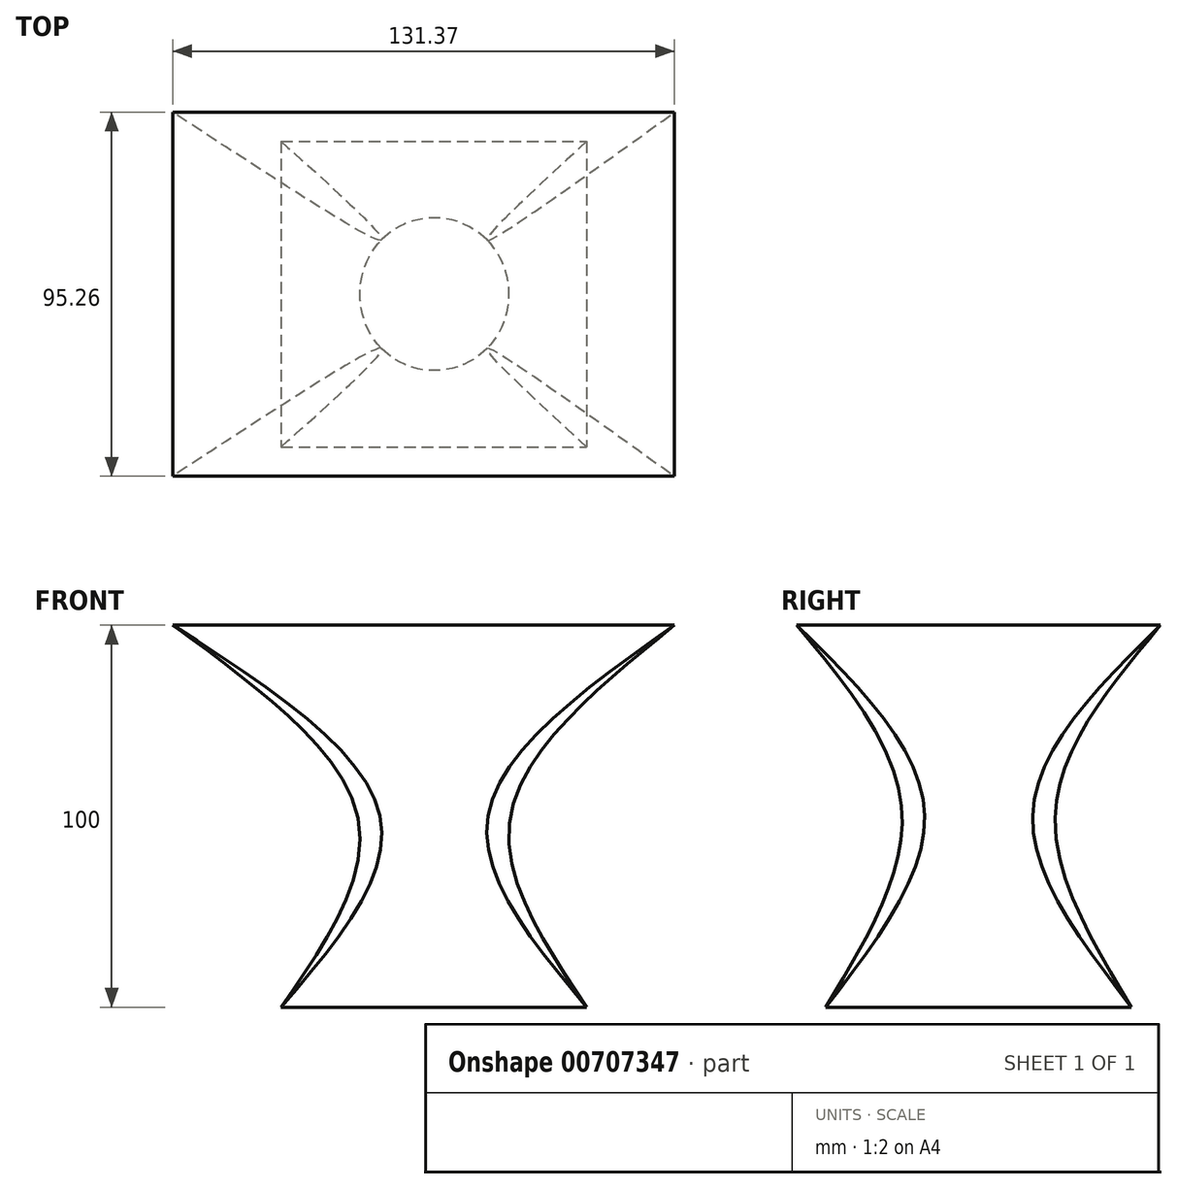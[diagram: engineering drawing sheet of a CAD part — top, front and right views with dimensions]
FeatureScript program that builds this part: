
annotation { "Feature Type Name" : "Feature", "Feature Type Description" : "" }
export const myFeature = defineFeature(function(context is Context, id is Id, definition is map)
    precondition{}
    {
        {
            var Q0;
            Q0=qCreatedBy(makeId("Top.planeOp"),FACE);
            var sketch = newSketch(context, id + "F0", { "sketchPlane" : qUnion([Q0])});
            skLineSegment(sketch, "E0.bottom", {"start": v(-40, 40) * mm, "end": v(40, 40) * mm});
            skLineSegment(sketch, "E0.top", {"start": v(-40, -40) * mm, "end": v(40, -40) * mm});
            skLineSegment(sketch, "E0.left", {"start": v(-40, 40) * mm, "end": v(-40, -40) * mm});
            skLineSegment(sketch, "E0.right", {"start": v(40, 40) * mm, "end": v(40, -40) * mm});
            skSolve(sketch);
        }
        {
            var Q0;
            Q0=qCreatedBy(makeId("Top.planeOp"),FACE);
            cPlane(context, id + "F1", {"entities" : qUnion([Q0]), "cplaneType" : CPlaneType.OFFSET, "offset" : 50 * mm, "width" : 150 * mm, "height" : 150 * mm});
        }
        {
            var Q0;
            Q0=qCreatedBy(id+"F1.planeOp",FACE);
            var sketch = newSketch(context, id + "F2", { "sketchPlane" : qUnion([Q0])});
            skCircle(sketch, "E1", {"center": v(0, 0) * mm, "radius": 20 * mm});
            skSolve(sketch);
        }
        {
            var Q0;
            Q0=qCreatedBy(id+"F1.planeOp",FACE);
            cPlane(context, id + "F3", {"entities" : qUnion([Q0]), "cplaneType" : CPlaneType.OFFSET, "offset" : 50 * mm, "width" : 150 * mm, "height" : 150 * mm});
        }
        {
            var Q0;
            Q0=qCreatedBy(id+"F3.planeOp",FACE);
            var sketch = newSketch(context, id + "F4", { "sketchPlane" : qUnion([Q0])});
            skLineSegment(sketch, "E2.bottom", {"start": v(-68.36, -47.63) * mm, "end": v(63, -47.63) * mm});
            skLineSegment(sketch, "E2.top", {"start": v(-68.36, 47.63) * mm, "end": v(63, 47.63) * mm});
            skLineSegment(sketch, "E2.left", {"start": v(-68.36, -47.63) * mm, "end": v(-68.36, 47.63) * mm});
            skLineSegment(sketch, "E2.right", {"start": v(63, -47.63) * mm, "end": v(63, 47.63) * mm});
            skSolve(sketch);
        }
        {
            var Q0;
            Q0=makeQuery(id+"F0.imprint","IMPRINT",FACE,{"disambiguationData":[TD([[makeQuery(id+"F0.imprint","IMPRINT",EDGE,{"derivedFrom":sQuery(id+"F0.wireOp",EDGE,"E0.bottom")}),-1.0]])]});
            var Q1;
            Q1=makeQuery(id+"F2.imprint","IMPRINT",FACE,{"disambiguationData":[TD([[makeQuery(id+"F2.imprint","IMPRINT",EDGE,{"derivedFrom":sQuery(id+"F2.wireOp",EDGE,"E1")}),1.0]])]});
            var Q2;
            Q2=makeQuery(id+"F4.imprint","IMPRINT",FACE,{"disambiguationData":[TD([[makeQuery(id+"F4.imprint","IMPRINT",EDGE,{"derivedFrom":sQuery(id+"F4.wireOp",EDGE,"E2.bottom")}),1.0]])]});
            loft(context, id + "F5", {"sheetProfilesArray" : [{ "sheetProfileEntities" : qUnion([Q0]) }, { "sheetProfileEntities" : qUnion([Q1]) }, { "sheetProfileEntities" : qUnion([Q2]) }]});
        }
    });
